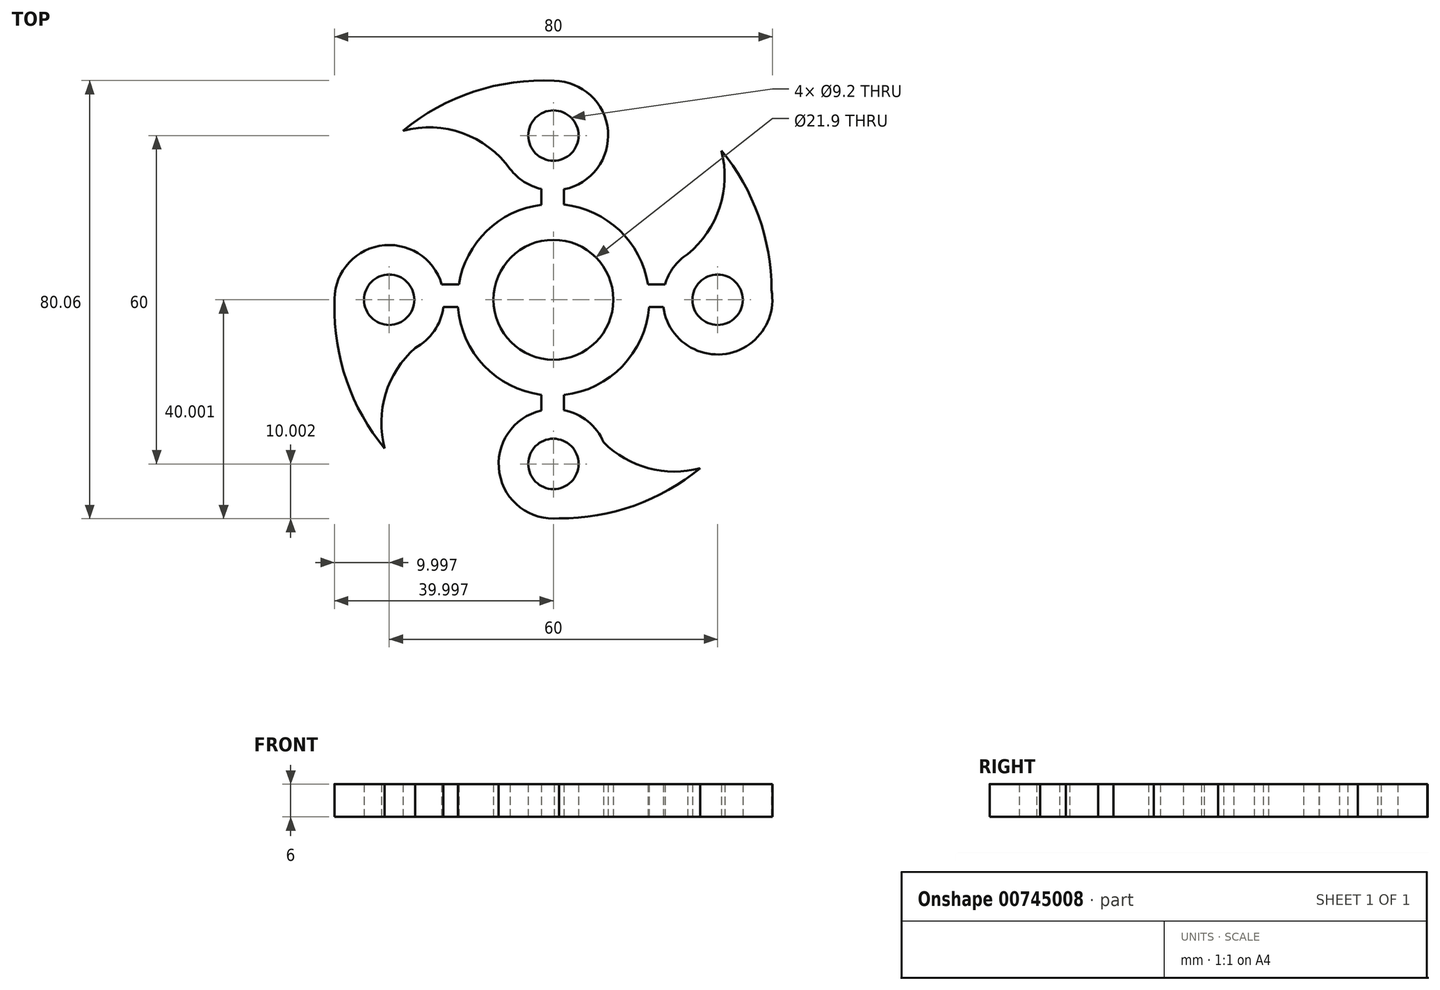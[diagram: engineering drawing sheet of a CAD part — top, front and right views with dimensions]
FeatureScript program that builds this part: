
annotation { "Feature Type Name" : "Feature", "Feature Type Description" : "" }
export const myFeature = defineFeature(function(context is Context, id is Id, definition is map)
    precondition{}
    {
        {
            var Q0;
            Q0=qCreatedBy(makeId("Top.planeOp"),FACE);
            var sketch = newSketch(context, id + "F0", { "sketchPlane" : qUnion([Q0])});
            skCircle(sketch, "E0", {"center": v(-24.23, 38.66) * mm, "radius": 4.6 * mm});
            skCircle(sketch, "E1", {"center": v(5.77, 8.66) * mm, "radius": 4.6 * mm});
            skCircle(sketch, "E2", {"center": v(-54.23, 8.66) * mm, "radius": 4.6 * mm});
            skCircle(sketch, "E3", {"center": v(-24.23, -21.34) * mm, "radius": 4.6 * mm});
            skPoint(sketch, "E4.start.orphan", {"position": v(-24.23, 30.66) * mm});
            skPoint(sketch, "E5.orphan", {"position": v(-46.23, 8.66) * mm});
            skLineSegment(sketch, "E6.trimOffspring", {"start": v(-33.75, 3.66) * mm, "end": v(-33.97, 3.66) * mm});
            skCircle(sketch, "E7", {"center": v(-24.23, 8.66) * mm, "radius": 10.95 * mm});
            skLineSegment(sketch, "E8", {"start": v(-6.96, 11.45) * mm, "end": v(-3.84, 11.45) * mm});
            skLineSegment(sketch, "E9", {"start": v(-6.78, 7.34) * mm, "end": v(-4.15, 7.34) * mm});
            skLineSegment(sketch, "E10", {"start": v(-41.68, 7.34) * mm, "end": v(-44.32, 7.34) * mm});
            skLineSegment(sketch, "E11", {"start": v(-41.5, 11.45) * mm, "end": v(-44.63, 11.45) * mm});
            skLineSegment(sketch, "E12", {"start": v(-22.3, -8.73) * mm, "end": v(-22.3, -11.53) * mm});
            skLineSegment(sketch, "E13", {"start": v(-26.44, -8.7) * mm, "end": v(-26.44, -11.58) * mm});
            skLineSegment(sketch, "E14", {"start": v(-26.44, 26.02) * mm, "end": v(-26.44, 28.9) * mm});
            skLineSegment(sketch, "E15", {"start": v(-22.3, 26.06) * mm, "end": v(-22.3, 28.85) * mm});
            skArc(sketch, "E16", {"start": v(-44.63, 11.45) * mm, "mid": v(-56.02, 18.5) * mm, "end": v(-64.2, 7.9) * mm});
            skArc(sketch, "E17", {"start": v(-22.3, 28.85) * mm, "mid": v(-14.27, 39.56) * mm, "end": v(-24.09, 48.66) * mm});
            skArc(sketch, "E18", {"start": v(-4.15, 7.34) * mm, "mid": v(7.31, -1.22) * mm, "end": v(15.6, 10.44) * mm});
            skArc(sketch, "E19", {"start": v(-26.44, -11.58) * mm, "mid": v(-34.1, -22.97) * mm, "end": v(-23.2, -31.28) * mm});
            skPoint(sketch, "E20.orphan", {"position": v(1.36, 7.34) * mm});
            skArc(sketch, "E21", {"start": v(-6.96, 11.45) * mm, "mid": v(-12.17, 21.34) * mm, "end": v(-22.3, 26.06) * mm});
            skArc(sketch, "E22.trimOffspring", {"start": v(-41.68, 7.34) * mm, "mid": v(-36.92, -3.4) * mm, "end": v(-26.44, -8.7) * mm});
            skArc(sketch, "E23.trimOffspring", {"start": v(-22.3, -8.73) * mm, "mid": v(-11.65, -3.5) * mm, "end": v(-6.78, 7.34) * mm});
            skArc(sketch, "E24.trimOffspring", {"start": v(-26.44, 26.02) * mm, "mid": v(-36.4, 21.24) * mm, "end": v(-41.5, 11.45) * mm});
            skPoint(sketch, "E25.orphan", {"position": v(-35.1, 7.34) * mm});
            skPoint(sketch, "E26.orphan", {"position": v(-34.82, 11.45) * mm});
            skPoint(sketch, "E27.orphan", {"position": v(-26.44, 19.39) * mm});
            skPoint(sketch, "E28.orphan", {"position": v(-22.3, 19.44) * mm});
            skPoint(sketch, "E29.orphan", {"position": v(-13.64, 11.45) * mm});
            skPoint(sketch, "E30.orphan", {"position": v(-22.3, -2.12) * mm});
            skPoint(sketch, "E31.orphan", {"position": v(-26.44, -2.06) * mm});
            skArc(sketch, "E32", {"start": v(-24.09, 48.66) * mm, "mid": v(-38.74, 46.7) * mm, "end": v(-51.69, 39.55) * mm});
            skArc(sketch, "E33", {"start": v(-32.14, 32.54) * mm, "mid": v(-40.82, 39.1) * mm, "end": v(-51.69, 39.55) * mm});
            skArc(sketch, "E34", {"start": v(15.6, 10.44) * mm, "mid": v(13.25, 23.98) * mm, "end": v(6.44, 35.92) * mm});
            skArc(sketch, "E35", {"start": v(0.27, 17.02) * mm, "mid": v(6.16, 25.56) * mm, "end": v(6.44, 35.92) * mm});
            skArc(sketch, "E36", {"start": v(-25.03, -31.23) * mm, "mid": v(-10.38, -29.27) * mm, "end": v(2.56, -22.12) * mm});
            skArc(sketch, "E37", {"start": v(-15.04, -17.4) * mm, "mid": v(-6.87, -22.11) * mm, "end": v(2.56, -22.12) * mm});
            skArc(sketch, "E38", {"start": v(-64.2, 7.9) * mm, "mid": v(-62, -6.15) * mm, "end": v(-55.05, -18.54) * mm});
            skArc(sketch, "E39", {"start": v(-49.48, -0.14) * mm, "mid": v(-54.88, -8.54) * mm, "end": v(-55.05, -18.54) * mm});
            skArc(sketch, "E40.trimOffspring", {"start": v(-49.48, -0.14) * mm, "mid": v(-46, 2.98) * mm, "end": v(-44.32, 7.34) * mm});
            skArc(sketch, "E41.trimOffspring", {"start": v(-32.14, 32.54) * mm, "mid": v(-29.6, 30.23) * mm, "end": v(-26.44, 28.9) * mm});
            skArc(sketch, "E42.trimOffspring", {"start": v(0.27, 17.02) * mm, "mid": v(-2.28, 14.6) * mm, "end": v(-3.84, 11.45) * mm});
            skArc(sketch, "E43.trimOffspring", {"start": v(-15.04, -17.4) * mm, "mid": v(-17.95, -13.56) * mm, "end": v(-22.3, -11.53) * mm});
            skSolve(sketch);
        }
        {
            var Q0;
            Q0=makeQuery(id+"F0.imprint","IMPRINT",FACE,{"disambiguationData":[TD([[makeQuery(id+"F0.imprint","IMPRINT",EDGE,{"derivedFrom":sQuery(id+"F0.wireOp",EDGE,"E0")}),-1.0]])]});
            extrude(context, id + "F1", {"entities" : qUnion([Q0]), "depth" : 6 * mm, "offsetDistance" : 25 * mm});
        }
    });
